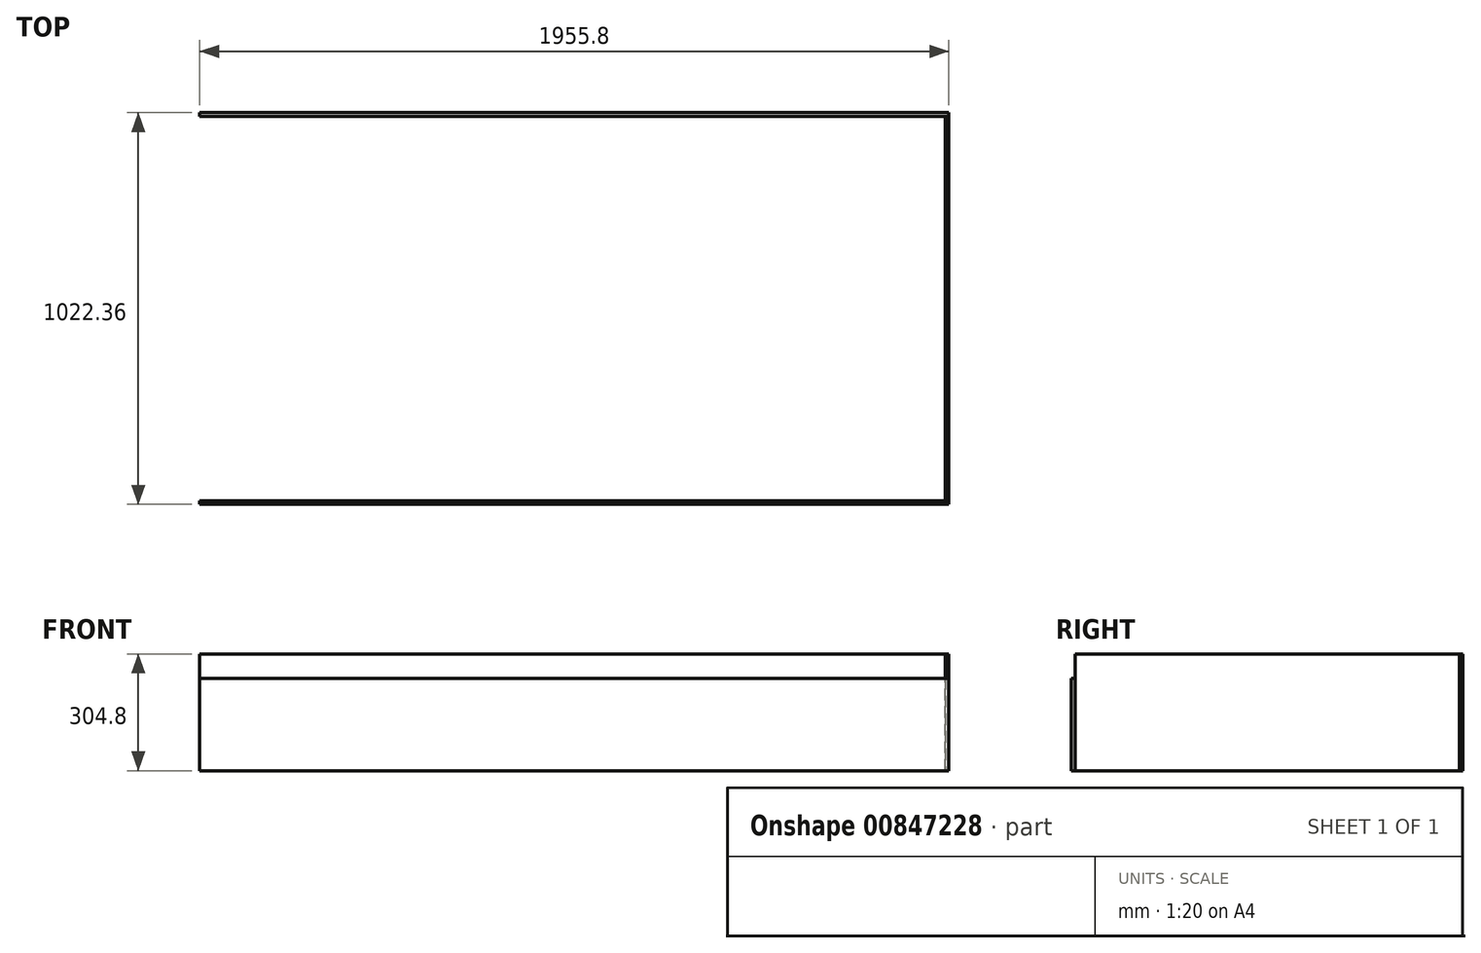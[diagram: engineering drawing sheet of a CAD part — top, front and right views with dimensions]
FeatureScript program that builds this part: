
annotation { "Feature Type Name" : "Feature", "Feature Type Description" : "" }
export const myFeature = defineFeature(function(context is Context, id is Id, definition is map)
    precondition{}
    {
        {
            var Q0;
            Q0=qCreatedBy(makeId("Front.planeOp"),FACE);
            var sketch = newSketch(context, id + "F0", { "sketchPlane" : qUnion([Q0])});
            skLineSegment(sketch, "E0.bottom", {"start": v(-977.9, 0) * mm, "end": v(0, 0) * mm});
            skLineSegment(sketch, "E0.top", {"start": v(-977.9, 304.8) * mm, "end": v(977.9, 304.8) * mm});
            skLineSegment(sketch, "E0.left", {"start": v(-977.9, 0) * mm, "end": v(-977.9, 304.8) * mm});
            skLineSegment(sketch, "E0.right", {"start": v(977.9, 0) * mm, "end": v(977.9, 304.8) * mm});
            skLineSegment(sketch, "E1", {"start": v(0, 0) * mm, "end": v(977.9, 0) * mm});
            skSolve(sketch);
        }
        {
            var Q0;
            Q0=makeQuery(id+"F0.imprint","IMPRINT",FACE,{"disambiguationData":[TD([[makeQuery(id+"F0.imprint","IMPRINT",EDGE,{"derivedFrom":sQuery(id+"F0.wireOp",EDGE,"E0.bottom")}),1.0]])]});
            extrude(context, id + "F1", {"entities" : qUnion([Q0]), "oppositeDirection" : true, "depth" : 9.52 * mm, "offsetDistance" : 25.4 * mm});
        }
        {
            var Q0;
            Q0=qCreatedBy(makeId("Front.planeOp"),FACE);
            cPlane(context, id + "F2", {"entities" : qUnion([Q0]), "cplaneType" : CPlaneType.OFFSET, "offset" : 1003.3 * mm, "width" : 152.4 * mm, "height" : 152.4 * mm});
        }
        {
            var Q0;
            Q0=qCreatedBy(id+"F2.planeOp",FACE);
            var sketch = newSketch(context, id + "F3", { "sketchPlane" : qUnion([Q0])});
            skLineSegment(sketch, "E2.0", {"start": v(977.9, 0) * mm, "end": v(-977.9, 0) * mm});
            skLineSegment(sketch, "E3", {"start": v(-977.9, 0) * mm, "end": v(-977.9, 241.3) * mm});
            skLineSegment(sketch, "E4", {"start": v(-977.9, 241.3) * mm, "end": v(977.9, 241.3) * mm});
            skLineSegment(sketch, "E5", {"start": v(977.9, 241.3) * mm, "end": v(977.9, 0) * mm});
            skSolve(sketch);
        }
        {
            var Q0;
            Q0=makeQuery(id+"F3.imprint","IMPRINT",FACE,{"disambiguationData":[TD([[makeQuery(id+"F3.imprint","IMPRINT",EDGE,{"derivedFrom":sQuery(id+"F3.wireOp",EDGE,"E2.0")}),-1.0]])]});
            extrude(context, id + "F4", {"entities" : qUnion([Q0]), "depth" : 9.52 * mm, "offsetDistance" : 25.4 * mm});
        }
        {
            var Q0;
            Q0=makeQuery(id+"F4.opExtrude","CAP_VERTEX",VERTEX,{"disambiguationData":[OSD([sQuery(id+"F3.wireOp",EDGE,"E2.0"),sQuery(id+"F3.wireOp",EDGE,"E5")])],"isStart":true});
            var Q1;
            Q1=makeQuery(id+"F4.opExtrude","CAP_VERTEX",VERTEX,{"disambiguationData":[OSD([sQuery(id+"F3.wireOp",EDGE,"E4"),sQuery(id+"F3.wireOp",EDGE,"E5")])],"isStart":true});
            var Q2;
            Q2=makeQuery(id+"F1.opExtrude","CAP_VERTEX",VERTEX,{"disambiguationData":[OSD([sQuery(id+"F0.wireOp",EDGE,"E0.right"),sQuery(id+"F0.wireOp",EDGE,"E1")])],"isStart":true});
            cPlane(context, id + "F5", {"entities" : qUnion([Q0, Q1, Q2]), "cplaneType" : CPlaneType.THREE_POINT, "offset" : 25.4 * mm, "width" : 152.4 * mm, "height" : 152.4 * mm});
        }
        {
            var Q0;
            Q0=qCreatedBy(id+"F5.planeOp",FACE);
            var sketch = newSketch(context, id + "F6", { "sketchPlane" : qUnion([Q0])});
            skPoint(sketch, "E6.0", {"position": v(-1003.3, 0) * mm});
            skPoint(sketch, "E7.0", {"position": v(0, 304.8) * mm});
            skLineSegment(sketch, "E8", {"start": v(0, 0) * mm, "end": v(0, 304.8) * mm});
            skLineSegment(sketch, "E9", {"start": v(0, 0) * mm, "end": v(-1003.3, 0) * mm});
            skLineSegment(sketch, "E10", {"start": v(-1003.3, 304.8) * mm, "end": v(0, 304.8) * mm});
            skLineSegment(sketch, "E11", {"start": v(-1003.3, 304.8) * mm, "end": v(-1003.3, 0) * mm});
            skSolve(sketch);
        }
        {
            var Q0;
            Q0 = qSketchRegion(id + "F6", true);
            extrude(context, id + "F7", {"entities" : qUnion([Q0]), "oppositeDirection" : true, "depth" : 9.52 * mm, "offsetDistance" : 25.4 * mm});
        }
    });
